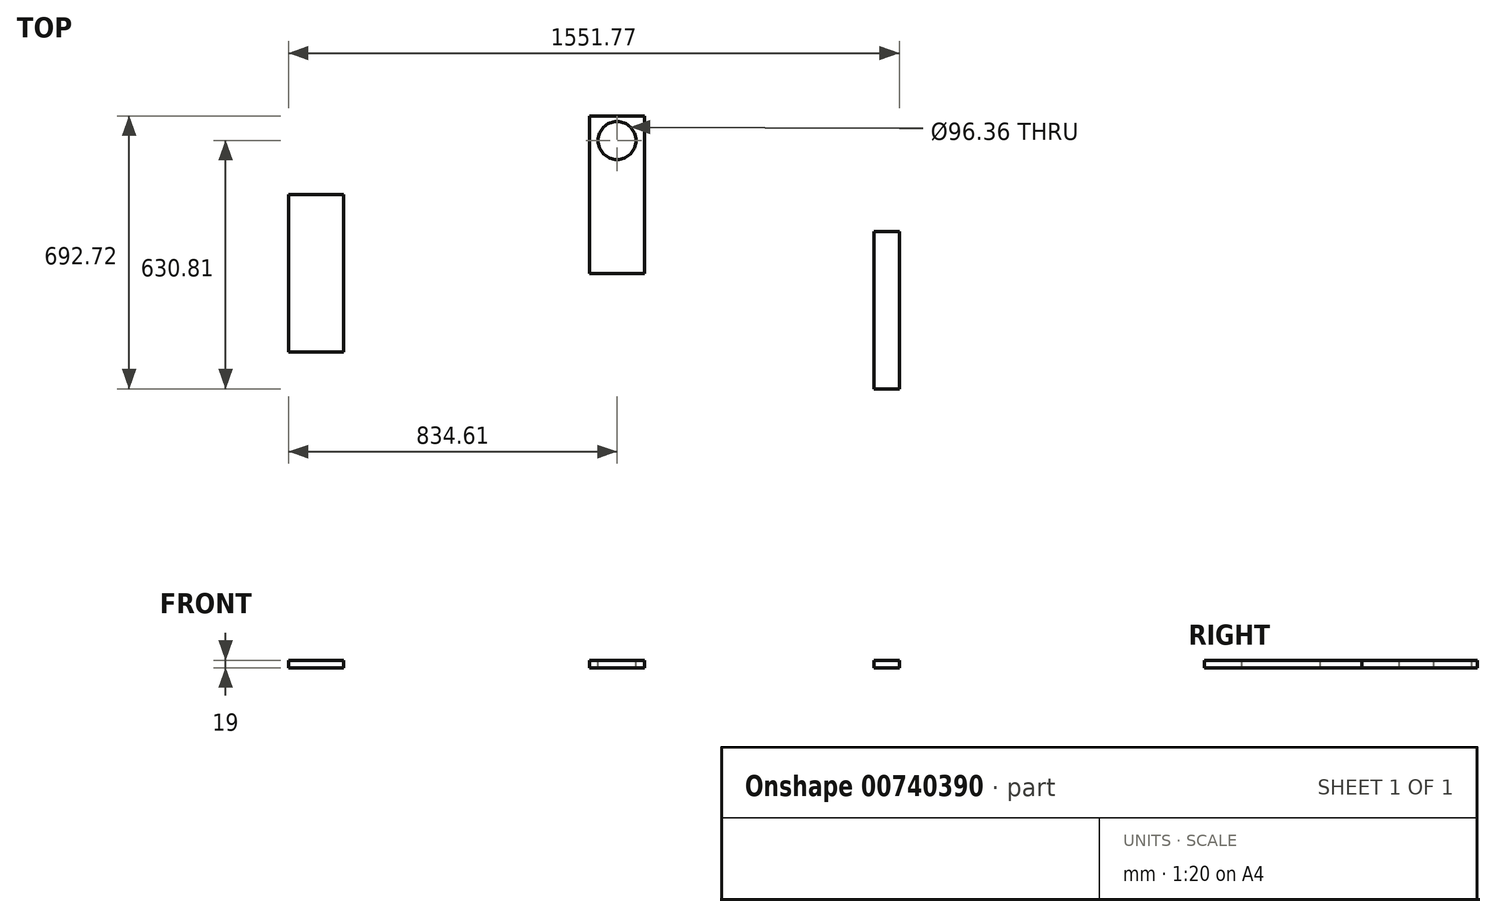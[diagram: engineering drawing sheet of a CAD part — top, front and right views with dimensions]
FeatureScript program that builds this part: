
annotation { "Feature Type Name" : "Feature", "Feature Type Description" : "" }
export const myFeature = defineFeature(function(context is Context, id is Id, definition is map)
    precondition{}
    {
        {
            var Q0;
            Q0=qCreatedBy(makeId("Top.planeOp"),FACE);
            var sketch = newSketch(context, id + "F0", { "sketchPlane" : qUnion([Q0])});
            skLineSegment(sketch, "E0.bottom", {"start": v(-307.02, 61.9) * mm, "end": v(-167.02, 61.9) * mm});
            skLineSegment(sketch, "E0.top", {"start": v(-307.02, -338.1) * mm, "end": v(-167.02, -338.1) * mm});
            skLineSegment(sketch, "E0.left", {"start": v(-307.02, 61.9) * mm, "end": v(-307.02, -338.1) * mm});
            skLineSegment(sketch, "E0.right", {"start": v(-167.02, 61.9) * mm, "end": v(-167.02, -338.1) * mm});
            skSolve(sketch);
        }
        {
            var Q0;
            Q0=qCreatedBy(makeId("Top.planeOp"),FACE);
            var sketch = newSketch(context, id + "F1", { "sketchPlane" : qUnion([Q0])});
            skLineSegment(sketch, "E1.bottom", {"start": v(-1071.63, -137.4) * mm, "end": v(-931.63, -137.4) * mm});
            skLineSegment(sketch, "E1.top", {"start": v(-1071.63, -537.4) * mm, "end": v(-931.63, -537.4) * mm});
            skLineSegment(sketch, "E1.left", {"start": v(-1071.63, -137.4) * mm, "end": v(-1071.63, -537.4) * mm});
            skLineSegment(sketch, "E1.right", {"start": v(-931.63, -137.4) * mm, "end": v(-931.63, -537.4) * mm});
            skSolve(sketch);
        }
        {
            var Q0;
            Q0=makeQuery(id+"F1.imprint","IMPRINT",FACE,{"disambiguationData":[TD([[makeQuery(id+"F1.imprint","IMPRINT",EDGE,{"derivedFrom":sQuery(id+"F1.wireOp",EDGE,"E1.bottom")}),-1.0]])]});
            extrude(context, id + "F2", {"entities" : qUnion([Q0]), "depth" : 19 * mm, "offsetDistance" : 25 * mm});
        }
        {
            var Q0;
            Q0=makeQuery(id+"F0.imprint","IMPRINT",FACE,{"disambiguationData":[TD([[makeQuery(id+"F0.imprint","IMPRINT",EDGE,{"derivedFrom":sQuery(id+"F0.wireOp",EDGE,"E0.bottom")}),-1.0]])]});
            extrude(context, id + "F3", {"entities" : qUnion([Q0]), "depth" : 19 * mm, "offsetDistance" : 25 * mm});
        }
        {
            var Q0;
            Q0=qCreatedBy(makeId("Top.planeOp"),FACE);
            var sketch = newSketch(context, id + "F4", { "sketchPlane" : qUnion([Q0])});
            skLineSegment(sketch, "E2.bottom", {"start": v(415.14, -230.81) * mm, "end": v(480.14, -230.81) * mm});
            skLineSegment(sketch, "E2.top", {"start": v(415.14, -630.81) * mm, "end": v(480.14, -630.81) * mm});
            skLineSegment(sketch, "E2.left", {"start": v(415.14, -230.81) * mm, "end": v(415.14, -630.81) * mm});
            skLineSegment(sketch, "E2.right", {"start": v(480.14, -230.81) * mm, "end": v(480.14, -630.81) * mm});
            skSolve(sketch);
        }
        {
            var Q0;
            Q0=makeQuery(id+"F4.imprint","IMPRINT",FACE,{"disambiguationData":[TD([[makeQuery(id+"F4.imprint","IMPRINT",EDGE,{"derivedFrom":sQuery(id+"F4.wireOp",EDGE,"E2.bottom")}),-1.0]])]});
            extrude(context, id + "F5", {"entities" : qUnion([Q0]), "depth" : 19 * mm, "offsetDistance" : 25 * mm});
        }
        {
            var Q0;
            Q0=makeQuery(id+"F3.opExtrude","CAP_FACE",FACE,{"disambiguationData":[OSD([sQuery(id+"F0.wireOp",EDGE,"E0.bottom"),sQuery(id+"F0.wireOp",EDGE,"E0.top"),sQuery(id+"F0.wireOp",EDGE,"E0.left"),sQuery(id+"F0.wireOp",EDGE,"E0.right")])],"isStart":false});
            var sketch = newSketch(context, id + "F6", { "sketchPlane" : qUnion([Q0])});
            skCircle(sketch, "E3", {"center": v(-237.02, 0) * mm, "radius": 48.18 * mm});
            skPoint(sketch, "E3.centerSnap0", {"position": v(-237.02, 61.9) * mm});
            skSolve(sketch);
        }
        {
            var Q0;
            Q0=makeQuery(id+"F6.imprint","IMPRINT",FACE,{"disambiguationData":[TD([[makeQuery(id+"F6.imprint","IMPRINT",EDGE,{"derivedFrom":sQuery(id+"F6.wireOp",EDGE,"E3")}),1.0]])]});
            extrude(context, id + "F7", {"entities" : qUnion([Q0]), "operationType" : NewBodyOperationType.REMOVE, "oppositeDirection" : true, "depth" : 19 * mm, "offsetDistance" : 25 * mm});
        }
    });
